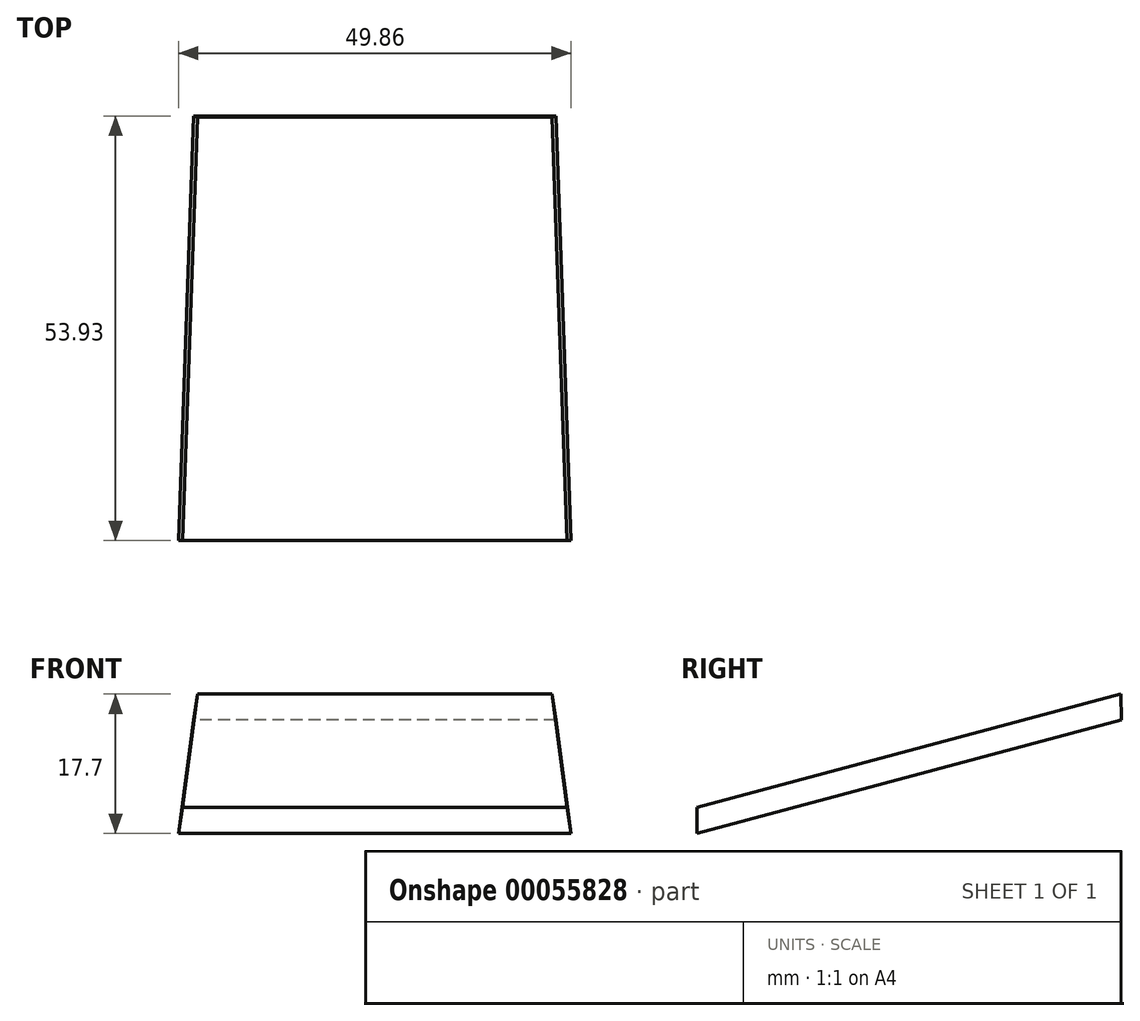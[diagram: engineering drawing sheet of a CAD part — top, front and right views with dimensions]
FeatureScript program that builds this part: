
annotation { "Feature Type Name" : "Feature", "Feature Type Description" : "" }
export const myFeature = defineFeature(function(context is Context, id is Id, definition is map)
    precondition{}
    {
        {
            var Q0;
            Q0=qCreatedBy(makeId("Front.planeOp"),FACE);
            var sketch = newSketch(context, id + "F0", { "sketchPlane" : qUnion([Q0])});
            skLineSegment(sketch, "E0", {"start": v(-28.55, 98.43) * mm, "end": v(28.55, 98.43) * mm, "construction": true});
            skLineSegment(sketch, "E1", {"start": v(-31.75, 98.43) * mm, "end": v(-43.84, 0) * mm});
            skLineSegment(sketch, "E2", {"start": v(31.75, 98.42) * mm, "end": v(43.84, 0) * mm, "construction": true});
            skLineSegment(sketch, "E3", {"start": v(-28.55, 98.43) * mm, "end": v(-29.04, 94.46) * mm, "construction": true});
            skLineSegment(sketch, "E4", {"start": v(29.04, 94.46) * mm, "end": v(28.55, 98.43) * mm, "construction": true});
            skLineSegment(sketch, "E5", {"start": v(-31.75, 98.43) * mm, "end": v(-28.55, 98.43) * mm, "construction": true});
            skLineSegment(sketch, "E6", {"start": v(28.55, 98.43) * mm, "end": v(31.75, 98.43) * mm, "construction": true});
            skLineSegment(sketch, "E7", {"start": v(-29.04, 94.46) * mm, "end": v(29.04, 94.46) * mm, "construction": true});
            skLineSegment(sketch, "E8", {"start": v(-28.55, 98.43) * mm, "end": v(-40.64, 0) * mm, "construction": true});
            skLineSegment(sketch, "E9", {"start": v(-31.75, 98.43) * mm, "end": v(31.75, 98.43) * mm});
            skLineSegment(sketch, "E10", {"start": v(40.64, 0) * mm, "end": v(29.04, 94.46) * mm, "construction": true});
            skLineSegment(sketch, "E11", {"start": v(31.75, 98.42) * mm, "end": v(43.84, 0) * mm});
            skLineSegment(sketch, "E12", {"start": v(-43.84, 0) * mm, "end": v(-36.67, 0) * mm});
            skLineSegment(sketch, "E13", {"start": v(-36.67, 0) * mm, "end": v(-22.98, 88.9) * mm});
            skLineSegment(sketch, "E14", {"start": v(-22.98, 88.9) * mm, "end": v(22.98, 88.9) * mm});
            skLineSegment(sketch, "E15", {"start": v(22.98, 88.9) * mm, "end": v(36.67, 0) * mm});
            skLineSegment(sketch, "E16", {"start": v(36.67, 0) * mm, "end": v(43.84, 0) * mm});
            skSolve(sketch);
        }
        {
            var Q0;
            Q0=qCreatedBy(makeId("Front.planeOp"),FACE);
            cPlane(context, id + "F1", {"entities" : qUnion([Q0]), "cplaneType" : CPlaneType.OFFSET, "offset" : 1.59 * mm, "width" : 152.4 * mm, "height" : 152.4 * mm});
        }
        {
            var Q0;
            Q0=qCreatedBy(id+"F1.planeOp",FACE);
            var sketch = newSketch(context, id + "F2", { "sketchPlane" : qUnion([Q0])});
            skLineSegment(sketch, "E17", {"start": v(0, 0) * mm, "end": v(-59.68, 0) * mm});
            skSolve(sketch);
        }
        {
            var Q0;
            Q0=sQuery(id+"F2.wireOp",EDGE,"E17");
            var Q1;
            Q1=qCreatedBy(id+"F1.planeOp",FACE);
            cPlane(context, id + "F3", {"entities" : qUnion([Q0, Q1]), "cplaneType" : CPlaneType.LINE_ANGLE, "offset" : 152.4 * mm, "angle" : 358 * degree, "width" : 152.4 * mm, "height" : 152.4 * mm});
        }
        {
            var Q0;
            Q0=qCreatedBy(id+"F3.planeOp",FACE);
            var sketch = newSketch(context, id + "F4", { "sketchPlane" : qUnion([Q0])});
            skLineSegment(sketch, "E18", {"start": v(-41.43, 0) * mm, "end": v(-27.07, 93.29) * mm});
            skLineSegment(sketch, "E19", {"start": v(-27.07, 93.29) * mm, "end": v(0, 93.29) * mm});
            skPoint(sketch, "E20.0", {"position": v(-36.67, 0) * mm});
            skLineSegment(sketch, "E21", {"start": v(-36.67, 0) * mm, "end": v(-41.43, 0) * mm});
            skLineSegment(sketch, "E22", {"start": v(-36.67, 0) * mm, "end": v(-23, 88.85) * mm});
            skLineSegment(sketch, "E23", {"start": v(-23, 88.85) * mm, "end": v(0, 88.85) * mm});
            skLineSegment(sketch, "E24", {"start": v(0, 0) * mm, "end": v(0, 97.14) * mm, "construction": true});
            skLineSegment(sketch, "E25.MirrorCS", {"start": v(36.67, 0) * mm, "end": v(41.43, 0) * mm});
            skLineSegment(sketch, "E26.MirrorCS", {"start": v(41.43, 0) * mm, "end": v(27.07, 93.29) * mm});
            skLineSegment(sketch, "E27.MirrorCS", {"start": v(36.67, 0) * mm, "end": v(23, 88.85) * mm});
            skLineSegment(sketch, "E28.MirrorCS", {"start": v(27.07, 93.29) * mm, "end": v(0, 93.29) * mm});
            skLineSegment(sketch, "E29.MirrorCS", {"start": v(23, 88.85) * mm, "end": v(0, 88.85) * mm});
            skSolve(sketch);
        }
        {
            var Q0;
            Q0=makeQuery(id+"F0.imprint","IMPRINT",FACE,{"disambiguationData":[TD([[makeQuery(id+"F0.imprint","IMPRINT",EDGE,{"derivedFrom":sQuery(id+"F0.wireOp",EDGE,"E1")}),1.0]])]});
            var Q1;
            Q1=makeQuery(id+"F4.imprint","IMPRINT",FACE,{"disambiguationData":[TD([[makeQuery(id+"F4.imprint","IMPRINT",EDGE,{"derivedFrom":sQuery(id+"F4.wireOp",EDGE,"E18")}),-1.0]])]});
            loft(context, id + "F5", {"sheetProfilesArray" : [{ "sheetProfileEntities" : qUnion([Q0]) }, { "sheetProfileEntities" : qUnion([Q1]) }]});
        }
        {
            var Q0;
            Q0=makeQuery(id+"F5.opLoft","CAP_FACE",FACE,{"disambiguationData":[OSD([makeQuery(id+"F4.imprint","IMPRINT",FACE,{"disambiguationData":[TD([[makeQuery(id+"F4.imprint","IMPRINT",EDGE,{"derivedFrom":sQuery(id+"F4.wireOp",EDGE,"E18")}),-1.0]])]})])],"isStart":true});
            var sketch = newSketch(context, id + "F6", { "sketchPlane" : qUnion([Q0])});
            skFitSpline(sketch, "E30.0", {"points": [v(-36.67, 0) * mm, v(-32.1, 29.62) * mm, v(-27.55, 59.23) * mm, v(-23, 88.85) * mm]});
            skLineSegment(sketch, "E31.0", {"start": v(-23, 88.85) * mm, "end": v(23, 88.85) * mm});
            skFitSpline(sketch, "E32.0", {"points": [v(23, 88.85) * mm, v(27.55, 59.23) * mm, v(32.1, 29.62) * mm, v(36.67, 0) * mm]});
            skLineSegment(sketch, "E33", {"start": v(-36.67, 0) * mm, "end": v(-33.5, 0) * mm});
            skLineSegment(sketch, "E34", {"start": v(-33.5, 0) * mm, "end": v(-20.69, 85.67) * mm});
            skLineSegment(sketch, "E35", {"start": v(-20.69, 85.67) * mm, "end": v(20.69, 85.67) * mm});
            skLineSegment(sketch, "E36", {"start": v(20.69, 85.67) * mm, "end": v(33.5, 0) * mm});
            skLineSegment(sketch, "E37", {"start": v(33.5, 0) * mm, "end": v(36.67, 0) * mm});
            skSolve(sketch);
        }
        {
            var Q0;
            Q0=qSketchRegion(id+"F6",true);
            var Q1;
            Q1=makeQuery(id+"F5.opLoft","CAP_FACE",FACE,{"disambiguationData":[OSD([makeQuery(id+"F0.imprint","IMPRINT",FACE,{"disambiguationData":[TD([[makeQuery(id+"F0.imprint","IMPRINT",EDGE,{"derivedFrom":sQuery(id+"F0.wireOp",EDGE,"E1")}),1.0]])]})])],"isStart":true});
            extrude(context, id + "F7", {"entities" : qUnion([Q0]), "operationType" : NewBodyOperationType.ADD, "depth" : 4.76 * mm, "hasSecondDirection" : true, "secondDirectionBound" : SecondDirectionBoundingType.UP_TO_SURFACE, "secondDirectionOppositeDirection" : true, "secondDirectionBoundEntityFace" : qUnion([Q1]), "secondDirectionDepth" : 25.4 * mm});
        }
        {
            var Q0;
            Q0=qCreatedBy(makeId("Right.planeOp"),FACE);
            var sketch = newSketch(context, id + "F8", { "sketchPlane" : qUnion([Q0])});
            skLineSegment(sketch, "E38.bottom", {"start": v(0, 0) * mm, "end": v(-7.34, 0) * mm});
            skLineSegment(sketch, "E38.top", {"start": v(0, -2.9) * mm, "end": v(-7.34, -2.9) * mm});
            skLineSegment(sketch, "E38.left", {"start": v(0, 0) * mm, "end": v(0, -2.9) * mm});
            skLineSegment(sketch, "E38.right", {"start": v(-7.34, 0) * mm, "end": v(-7.34, -2.9) * mm});
            skSolve(sketch);
        }
        {
            var Q0;
            Q0=makeQuery(id+"F8.imprint","IMPRINT",FACE,{"disambiguationData":[TD([[makeQuery(id+"F8.imprint","IMPRINT",EDGE,{"derivedFrom":sQuery(id+"F8.wireOp",EDGE,"E38.bottom")}),1.0]])]});
            extrude(context, id + "F9", {"entities" : qUnion([Q0]), "operationType" : NewBodyOperationType.REMOVE, "endBound" : BoundingType.THROUGH_ALL, "oppositeDirection" : true, "depth" : 25.4 * mm, "hasSecondDirection" : true, "secondDirectionBound" : SecondDirectionBoundingType.THROUGH_ALL, "secondDirectionOppositeDirection" : false, "secondDirectionDepth" : 25.4 * mm});
        }
        {
            var Q0;
            Q0=qCreatedBy(makeId("Right.planeOp"),FACE);
            var sketch = newSketch(context, id + "F10", { "sketchPlane" : qUnion([Q0])});
            skPoint(sketch, "E39.0", {"position": v(-4.69, 88.74) * mm});
            skPoint(sketch, "E40.0", {"position": v(-9.45, 88.57) * mm});
            skFitSpline(sketch, "E41.0", {"points": [v(-6.35, 0) * mm, v(-7.38, 29.52) * mm, v(-8.41, 59.05) * mm, v(-9.45, 88.57) * mm]});
            skFitSpline(sketch, "E42.0", {"points": [v(-9.45, 88.57) * mm, v(-7.86, 88.63) * mm, v(-6.27, 88.68) * mm, v(-4.69, 88.74) * mm]});
            skLineSegment(sketch, "E43", {"start": v(-4.69, 88.74) * mm, "end": v(-9.4, 87.47) * mm});
            skSolve(sketch);
        }
        {
            var Q0;
            Q0=qSketchRegion(id+"F10",true);
            extrude(context, id + "F11", {"entities" : qUnion([Q0]), "operationType" : NewBodyOperationType.REMOVE, "endBound" : BoundingType.THROUGH_ALL, "oppositeDirection" : true, "depth" : 25.4 * mm, "hasSecondDirection" : true, "secondDirectionBound" : SecondDirectionBoundingType.THROUGH_ALL, "secondDirectionOppositeDirection" : false, "secondDirectionDepth" : 25.4 * mm});
        }
        {
            var Q0;
            Q0=qCreatedBy(makeId("Right.planeOp"),FACE);
            var sketch = newSketch(context, id + "F12", { "sketchPlane" : qUnion([Q0])});
            skFitSpline(sketch, "E44.0", {"points": [v(-4.84, 93.17) * mm, v(-3.76, 62.12) * mm, v(-2.67, 31.06) * mm, v(-1.59, 0) * mm]});
            skLineSegment(sketch, "E45.0", {"start": v(-9.4, 87.47) * mm, "end": v(-4.69, 88.74) * mm});
            skLineSegment(sketch, "E46", {"start": v(-4.8, 92) * mm, "end": v(-58.62, 77.57) * mm});
            skLineSegment(sketch, "E47", {"start": v(-58.62, 77.57) * mm, "end": v(-58.62, 74.29) * mm});
            skLineSegment(sketch, "E48", {"start": v(-58.62, 74.29) * mm, "end": v(-9.4, 87.47) * mm});
            skSolve(sketch);
        }
        {
            var Q0;
            Q0 = qSketchRegion(id + "F12", true);
            var Q1;
            Q1=makeQuery(id+"F7.opExtrude","SWEPT_FACE",FACE,{"disambiguationData":[OSD([sQuery(id+"F6.wireOp",EDGE,"E32.0")])]});
            var Q2;
            Q2=makeQuery(id+"F7.opExtrude","SWEPT_FACE",FACE,{"disambiguationData":[OSD([sQuery(id+"F6.wireOp",EDGE,"E30.0")])]});
            extrude(context, id + "F13", {"entities" : qUnion([Q0]), "endBound" : BoundingType.UP_TO_SURFACE, "endBoundEntityFace" : qUnion([Q1]), "depth" : 25.4 * mm, "hasSecondDirection" : true, "secondDirectionBound" : SecondDirectionBoundingType.UP_TO_SURFACE, "secondDirectionOppositeDirection" : true, "secondDirectionBoundEntityFace" : qUnion([Q2]), "secondDirectionDepth" : 25.4 * mm});
        }
        {
            var Q0;
            Q0=makeQuery(id+"F5.opLoft","SWEPT_BODY",BODY,{"disambiguationData":[OSD([makeQuery(id+"F0.imprint","IMPRINT",FACE,{"disambiguationData":[TD([[makeQuery(id+"F0.imprint","IMPRINT",EDGE,{"derivedFrom":sQuery(id+"F0.wireOp",EDGE,"E1")}),1.0]])]}),makeQuery(id+"F4.imprint","IMPRINT",FACE,{"disambiguationData":[TD([[makeQuery(id+"F4.imprint","IMPRINT",EDGE,{"derivedFrom":sQuery(id+"F4.wireOp",EDGE,"E18")}),-1.0]])]})])]});
            deleteBodies(context, id + "F14", {"entities" : qUnion([Q0])});
        }
    });
